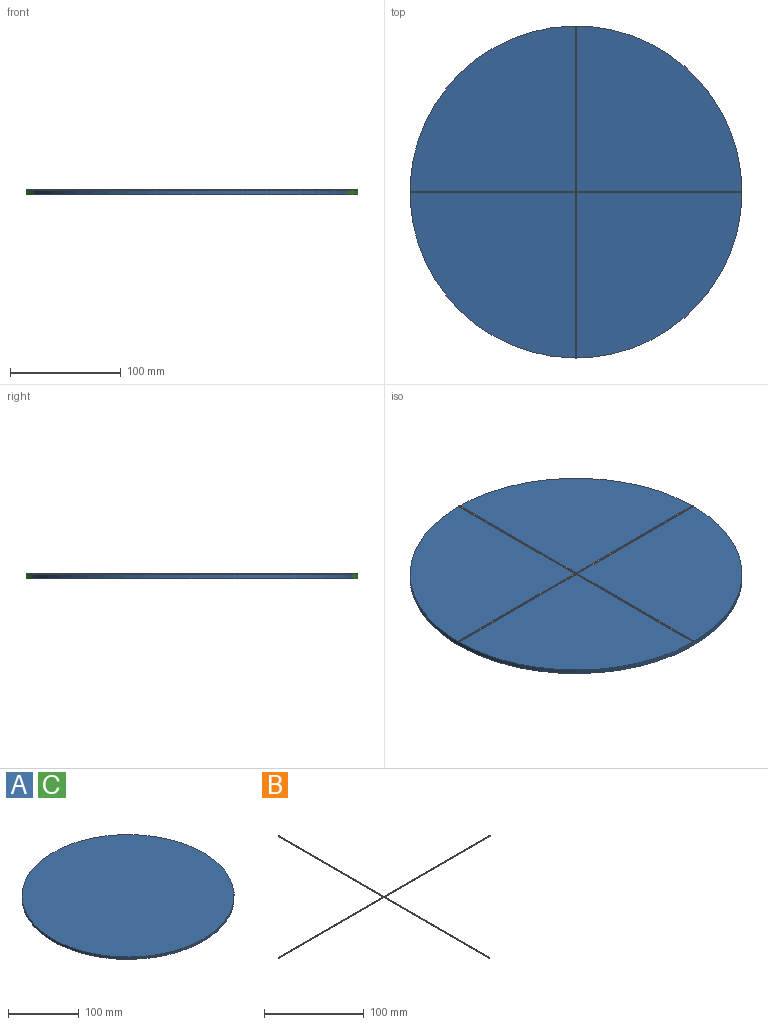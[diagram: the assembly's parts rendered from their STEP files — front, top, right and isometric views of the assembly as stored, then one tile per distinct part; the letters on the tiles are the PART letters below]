
ASSEMBLY  parts=3 mates=1
PART A: 3 faces, bbox 300x300x4 mm
  f0: cylinder r=150mm len=300mm, axis (0,0,-1), area 3769.9mm2, adj f1,f2
  f1: plane 300x300mm, normal (0,0,1), area 70685.8mm2, adj f0
  f2: plane 300x300mm, normal (0,0,-1), area 70685.8mm2, adj f0
PART B: 14 faces, bbox 300x300x1 mm
  f0: plane 1x1mm, normal (0,-1,0), area 1mm2, adj f1,f11,f12,f13
  f1: plane 149.5x1mm, normal (1,0,0), area 149.5mm2, adj f0,f2,f12,f13
  f2: plane 149.5x1mm, normal (0,-1,0), area 149.5mm2, adj f1,f3,f12,f13
  f3: plane 1x1mm, normal (1,0,0), area 1mm2, adj f2,f4,f12,f13
  f4: plane 149.5x1mm, normal (0,1,0), area 149.5mm2, adj f3,f5,f12,f13
  f5: plane 149.5x1mm, normal (1,0,0), area 149.5mm2, adj f4,f6,f12,f13
  f6: plane 1x1mm, normal (0,1,0), area 1mm2, adj f5,f7,f12,f13
  f7: plane 149.5x1mm, normal (-1,0,0), area 149.5mm2, adj f6,f8,f12,f13
  f8: plane 149.5x1mm, normal (0,1,0), area 149.5mm2, adj f7,f9,f12,f13
  f9: plane 1x1mm, normal (-1,0,0), area 1mm2, adj f8,f10,f12,f13
  f10: plane 149.5x1mm, normal (0,-1,0), area 149.5mm2, adj f9,f11,f12,f13
  f11: plane 149.5x1mm, normal (-1,0,0), area 149.5mm2, adj f0,f10,f12,f13
  f12: plane 300x300mm, normal (0,0,1), area 599mm2, adj f0,f1,f2,f3,f4,f5,f6,f7
  f13: plane 300x300mm, normal (0,0,-1), area 599mm2, adj f0,f1,f2,f3,f4,f5,f6,f7
PART C: same geometry as A
PLACE A t=(0.39,-0.17,-2.59)mm
PLACE B t=(0.39,-0.17,1.41)mm
PLACE C t=(0.39,-0.17,-2.59)mm
MATE fastened B.f13 <-> A.f0  axis (0,0,-1) through (0.39,-0.17,1.41)mm
